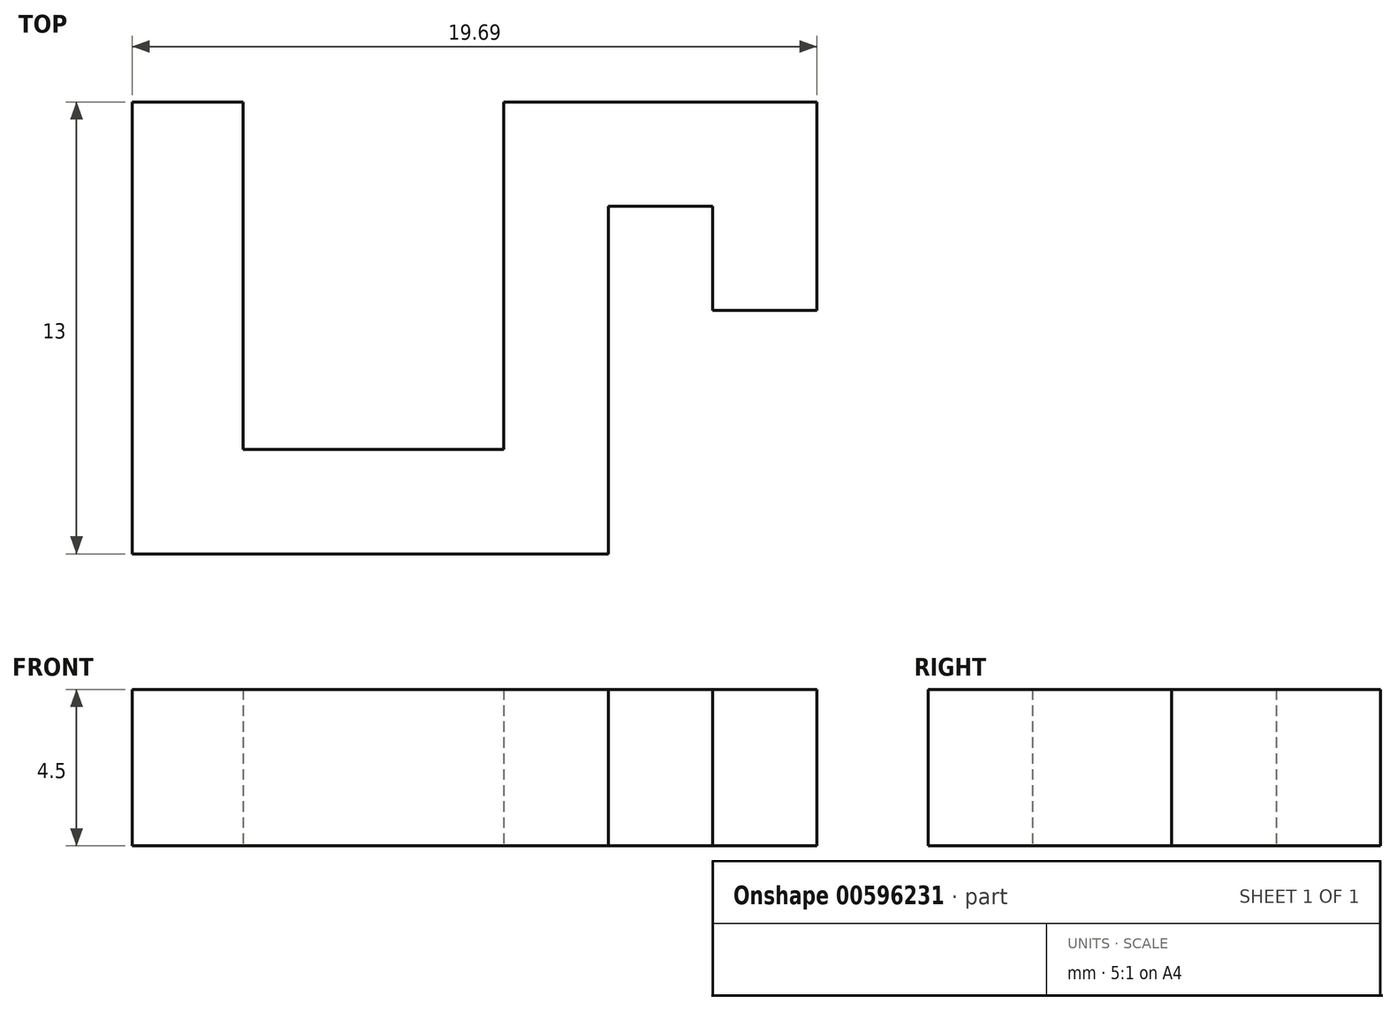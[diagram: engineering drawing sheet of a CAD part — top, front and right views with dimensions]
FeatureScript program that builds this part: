
annotation { "Feature Type Name" : "Feature", "Feature Type Description" : "" }
export const myFeature = defineFeature(function(context is Context, id is Id, definition is map)
    precondition{}
    {
        {
            var Q0;
            Q0=qCreatedBy(makeId("Top.planeOp"),FACE);
            var sketch = newSketch(context, id + "F0", { "sketchPlane" : qUnion([Q0])});
            skLineSegment(sketch, "E0", {"start": v(-45.4, 13) * mm, "end": v(-45.4, 3) * mm});
            skLineSegment(sketch, "E1", {"start": v(-45.4, 3) * mm, "end": v(-37.9, 3) * mm});
            skLineSegment(sketch, "E2", {"start": v(-37.9, 3) * mm, "end": v(-37.9, 13) * mm});
            skLineSegment(sketch, "E3", {"start": v(-45.4, 13) * mm, "end": v(-48.6, 13) * mm});
            skLineSegment(sketch, "E4", {"start": v(-48.6, 13) * mm, "end": v(-48.6, 0) * mm});
            skLineSegment(sketch, "E5", {"start": v(-48.6, 0) * mm, "end": v(-34.9, 0) * mm});
            skLineSegment(sketch, "E6", {"start": v(-34.9, 0) * mm, "end": v(-34.9, 10) * mm});
            skLineSegment(sketch, "E7", {"start": v(-34.9, 10) * mm, "end": v(-31.9, 10) * mm});
            skLineSegment(sketch, "E8", {"start": v(-31.9, 10) * mm, "end": v(-31.9, 7) * mm});
            skLineSegment(sketch, "E9", {"start": v(-31.9, 7) * mm, "end": v(-28.9, 7) * mm});
            skLineSegment(sketch, "E10", {"start": v(-28.9, 7) * mm, "end": v(-28.9, 13) * mm});
            skLineSegment(sketch, "E11", {"start": v(-28.9, 13) * mm, "end": v(-37.9, 13) * mm});
            skSolve(sketch);
        }
        {
            var Q0;
            Q0=makeQuery(id+"F0.imprint","IMPRINT",FACE,{"disambiguationData":[TD([[makeQuery(id+"F0.imprint","IMPRINT",EDGE,{"derivedFrom":sQuery(id+"F0.wireOp",EDGE,"E0")}),-1.0]])]});
            extrude(context, id + "F1", {"entities" : qUnion([Q0]), "depth" : 4.5 * mm, "offsetDistance" : 25 * mm});
        }
    });
